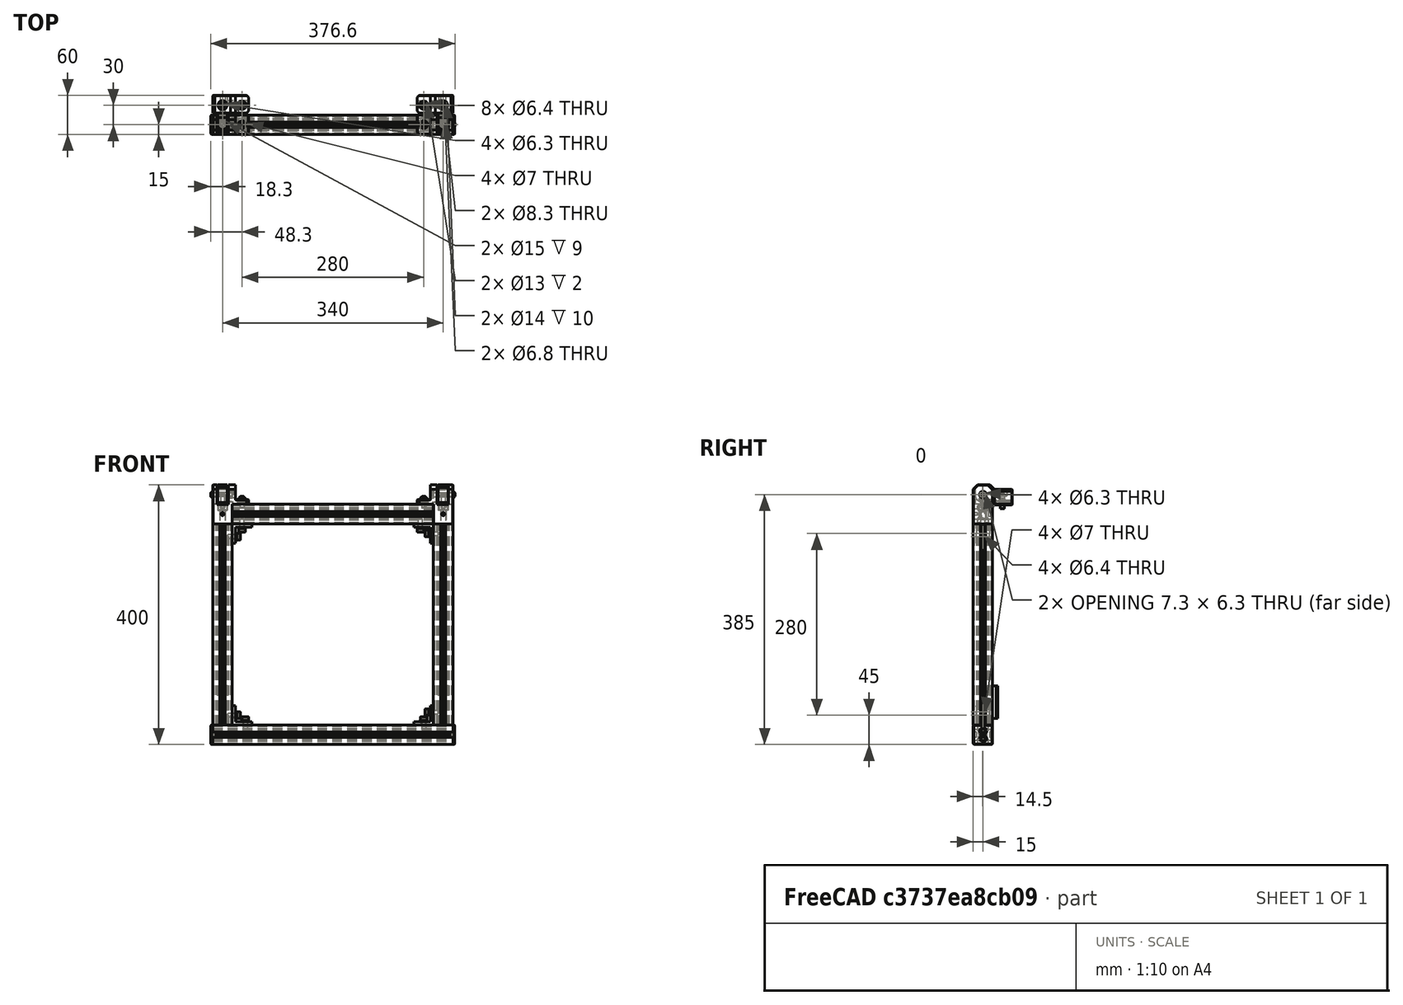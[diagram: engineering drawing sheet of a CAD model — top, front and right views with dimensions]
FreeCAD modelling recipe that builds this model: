
FCSTD DOCUMENT  (FreeCAD 0.19R24291 (Git))
Label: top-lid-assembly
License: Other
LicenseURL: GPL3
objects: Part::FeaturePython×32, Part::Feature×16, App::Part×1
note: 48 computed .brp shape members not serialized (recipe doc carries the construction recipe); baked Part::Feature solids carry a one-line shape summary decoded from their .brp

FEATURE [Part::Feature] Extrude002002003001  label="3030-370mm-top-lid-001"
  Placement = pos=(-3e-15,0,15) rot=(0,1,0;1.5708rad)
  shape: bbox 370 x 30 x 30 mm, 95 faces (baked)
FEATURE [Part::Feature] Extrude002002004001  label="3030-310mm-top-lid-001"
  Placement = pos=(15,0,30) rot=(0,0,1;0rad)
  shape: bbox 30 x 30 x 310 mm, 95 faces (baked)
FEATURE [Part::Feature] Extrude002002004002  label="3030-310mm-top-lid-002"
  Placement = pos=(355,0,30) rot=(0,0,1;0rad)
  shape: bbox 30 x 30 x 310 mm, 95 faces (baked)
FEATURE [Part::Feature] Extrude002002004003  label="3030-310mm-top-lid-003"
  Placement = pos=(340,0,355) rot=(0,-1,0;1.5708rad)
  shape: bbox 310 x 30 x 30 mm, 95 faces (baked)
FEATURE [Part::Feature] Chamfer002001010001
  Placement = pos=(30,45,385) rot=(0,0.707107,-0.707107;3.14159rad)
  shape: bbox 55 x 57 x 31 mm, 55 faces (baked)
FEATURE [Part::Feature] Chamfer002001012001
  Placement = pos=(30,15,370) rot=(0,0.707107,-0.707107;3.14159rad)
  shape: bbox 55 x 30 x 65 mm, 86 faces (baked)
FEATURE [Part::Feature] Part__Mirroring001001  label="Chamfer002001012001 (Mirror #2)001"
  Placement = pos=(340,15,370) rot=(0,0.707107,-0.707107;3.14159rad)
  shape: bbox 55 x 30 x 65 mm, 86 faces (baked)
FEATURE [Part::Feature] Part__Mirroring001002  label="Chamfer002001010001 (Mirror #1)001"
  Placement = pos=(340,45,385) rot=(0,0.707107,-0.707107;3.14159rad)
  shape: bbox 55 x 57 x 31 mm, 55 faces (baked)
FEATURE [Part::FeaturePython] Screw  label="M8x30-Screw"  # Fasteners workbench fastener (typed FeaturePython)
  Placement = pos=(355,1.23e-13,361) rot=(0,0,1;0rad)
  baseObject = -> Part__Mirroring001001 [Edge94]
  diameter = 8
  invert = false
  length = 6
  lengthCustom = 30
  matchOuter = true
  offset = 0
  thread = false
  type = 33
FEATURE [Part::FeaturePython] Screw001  label="M8x30-Screw001"  # Fasteners workbench fastener (typed FeaturePython)
  Placement = pos=(15,7.82e-14,361) rot=(0,0,1;0rad)
  baseObject = -> Chamfer002001012001 [Edge94]
  diameter = 8
  invert = true
  length = 6
  lengthCustom = 30
  matchOuter = true
  offset = 0
  thread = false
  type = 33
FEATURE [Part::FeaturePython] Washer  label="M6-Washer"  # Fasteners workbench fastener (typed FeaturePython)
  Placement = pos=(325,1.23e-13,377) rot=(0,0,1;0rad)
  baseObject = -> Part__Mirroring001001 [Edge130]
  diameter = 2
  invert = true
  matchOuter = true
  offset = 0
  type = 4
FEATURE [Part::FeaturePython] Washer001  label="M6-Washer001"  # Fasteners workbench fastener (typed FeaturePython)
  Placement = pos=(45,8.2e-14,377) rot=(0,0,1;0rad)
  baseObject = -> Chamfer002001012001 [Edge130]
  diameter = 2
  invert = false
  matchOuter = true
  offset = 0
  type = 4
FEATURE [Part::FeaturePython] Screw002  label="M6x14-Screw"  # Fasteners workbench fastener (typed FeaturePython)
  Placement = pos=(45,8.2e-14,378.8) rot=(0,0,1;0rad)
  baseObject = -> Washer001 [Edge1]
  diameter = 4
  invert = false
  length = 2
  lengthCustom = 14
  matchOuter = true
  offset = 0
  thread = false
  type = 39
FEATURE [Part::FeaturePython] Screw003  label="M6x14-Screw001"  # Fasteners workbench fastener (typed FeaturePython)
  Placement = pos=(325,1.23e-13,378.8) rot=(0,0,1;0rad)
  baseObject = -> Washer [Edge1]
  diameter = 4
  invert = false
  length = 2
  lengthCustom = 14
  matchOuter = true
  offset = 0
  thread = false
  type = 39
FEATURE [Part::FeaturePython] Nut  label="M6-Nut"  # Fasteners workbench fastener (typed FeaturePython)
  Placement = pos=(30,8.5e-14,385) rot=(0,-1,0;1.5708rad)
  baseObject = -> Chamfer002001012001 [Edge177]
  diameter = 8
  invert = false
  matchOuter = true
  offset = 0
  thread = false
  type = 7
FEATURE [Part::FeaturePython] Nut001  label="M6-Nut001"  # Fasteners workbench fastener (typed FeaturePython)
  Placement = pos=(340,1.28e-13,385) rot=(0,-1,0;1.5708rad)
  baseObject = -> Part__Mirroring001001 [Edge177]
  diameter = 8
  invert = false
  matchOuter = true
  offset = 0
  thread = false
  type = 7
FEATURE [Part::FeaturePython] Screw004  label="M6x10-Screw"  # Fasteners workbench fastener (typed FeaturePython)
  Placement = pos=(5e-14,8.5e-14,385) rot=(0,-1,0;1.5708rad)
  baseObject = -> Chamfer002001012001 [Edge70]
  diameter = 4
  invert = false
  length = 0
  lengthCustom = 10
  matchOuter = true
  offset = 0
  thread = false
  type = 39
FEATURE [Part::FeaturePython] Screw005  label="M6x10-Screw001"  # Fasteners workbench fastener (typed FeaturePython)
  Placement = pos=(370,1.32e-13,385) rot=(0,1,0;1.5708rad)
  baseObject = -> Part__Mirroring001001 [Edge70]
  diameter = 4
  invert = true
  length = 0
  lengthCustom = 10
  matchOuter = true
  offset = 0
  thread = false
  type = 39
FEATURE [Part::FeaturePython] Washer004  label="M6-Washer004"  # Fasteners workbench fastener (typed FeaturePython)
  Placement = pos=(325,30,374) rot=(0,0,1;0rad)
  baseObject = -> Part__Mirroring001002 [Edge130]
  diameter = 7
  invert = false
  matchOuter = true
  offset = 0
  type = 3
FEATURE [Part::FeaturePython] Washer005  label="M6-Washer005"  # Fasteners workbench fastener (typed FeaturePython)
  Placement = pos=(45,30,374) rot=(0,0,1;0rad)
  baseObject = -> Chamfer002001010001 [Edge130]
  diameter = 7
  invert = true
  matchOuter = true
  offset = 0
  type = 3
FEATURE [Part::FeaturePython] Screw008  label="M6x12-Screw"  # Fasteners workbench fastener (typed FeaturePython)
  Placement = pos=(325,30,375.8) rot=(0,0,1;0rad)
  baseObject = -> Washer004 [Edge1]
  diameter = 4
  invert = false
  length = 1
  lengthCustom = 12
  matchOuter = true
  offset = 0
  thread = false
  type = 39
FEATURE [Part::FeaturePython] Screw009  label="M6x12-Screw001"  # Fasteners workbench fastener (typed FeaturePython)
  Placement = pos=(45,30,375.8) rot=(0,0,1;0rad)
  baseObject = -> Washer005 [Edge1]
  diameter = 4
  invert = false
  length = 1
  lengthCustom = 12
  matchOuter = true
  offset = 0
  thread = false
  type = 39
FEATURE [Part::FeaturePython] Screw010  label="M6x20-Screw"  # Fasteners workbench fastener (typed FeaturePython)
  Placement = pos=(355,30,383) rot=(0,0,1;0rad)
  baseObject = -> Part__Mirroring001002 [Edge133]
  diameter = 4
  invert = false
  length = 4
  lengthCustom = 20
  matchOuter = true
  offset = 0
  thread = false
  type = 39
FEATURE [Part::FeaturePython] Screw011  label="M6x20-Screw001"  # Fasteners workbench fastener (typed FeaturePython)
  Placement = pos=(15,30,383) rot=(0,0,1;0rad)
  baseObject = -> Chamfer002001010001 [Edge133]
  diameter = 4
  invert = true
  length = 4
  lengthCustom = 20
  matchOuter = true
  offset = 0
  thread = false
  type = 39
FEATURE [Part::Feature] Part__Feature112001073  label="L-corner-bracket007"
  Placement = pos=(340,7.8e-14,340) rot=(0.57735,0.57735,-0.57735;4.18879rad)
  shape: bbox 30 x 20 x 30 mm, 10 faces (baked)
FEATURE [Part::Feature] Part__Feature112001074  label="L-corner-bracket008"
  Placement = pos=(30,7.8e-14,340) rot=(0.707107,0.707107,0;3.14159rad)
  shape: bbox 30 x 20 x 30 mm, 10 faces (baked)
FEATURE [Part::Feature] Part__Feature112001075  label="L-corner-bracket009"
  Placement = pos=(30,7.8e-14,30) rot=(0.57735,0.57735,0.57735;2.0944rad)
  shape: bbox 30 x 20 x 30 mm, 10 faces (baked)
FEATURE [Part::Feature] Part__Feature112001076  label="L-corner-bracket010"
  Placement = pos=(340,7.8e-14,30) rot=(0,0,1;1.5708rad)
  shape: bbox 30 x 20 x 30 mm, 10 faces (baked)
FEATURE [Part::FeaturePython] Washer006  label="M6-Washer006"  # Fasteners workbench fastener (typed FeaturePython)
  Placement = pos=(50,7.4e-14,35) rot=(0,0,1;0rad)
  baseObject = -> Part__Feature112001075 [Edge1]
  diameter = 2
  invert = true
  matchOuter = false
  offset = 0
  type = 4
FEATURE [Part::FeaturePython] Washer007  label="M6-Washer007"  # Fasteners workbench fastener (typed FeaturePython)
  Placement = pos=(35,7.7e-14,45) rot=(0,1,0;1.5708rad)
  baseObject = -> Part__Feature112001075 [Edge7]
  diameter = 2
  invert = true
  matchOuter = false
  offset = 0
  type = 4
FEATURE [Part::FeaturePython] Washer008  label="M6-Washer008"  # Fasteners workbench fastener (typed FeaturePython)
  Placement = pos=(325,7.5e-14,35) rot=(0,0,1;0rad)
  baseObject = -> Part__Feature112001076 [Edge7]
  diameter = 2
  invert = true
  matchOuter = false
  offset = 0
  type = 4
FEATURE [Part::FeaturePython] Washer009  label="M6-Washer009"  # Fasteners workbench fastener (typed FeaturePython)
  Placement = pos=(335,7.7e-14,50) rot=(0,-1,0;1.5708rad)
  baseObject = -> Part__Feature112001076 [Edge4]
  diameter = 2
  invert = true
  matchOuter = false
  offset = 0
  type = 4
FEATURE [Part::FeaturePython] Washer010  label="M6-Washer010"  # Fasteners workbench fastener (typed FeaturePython)
  Placement = pos=(320,7.9e-14,335) rot=(1,0,0;3.14159rad)
  baseObject = -> Part__Feature112001073 [Edge4]
  diameter = 2
  invert = true
  matchOuter = false
  offset = 0
  type = 4
FEATURE [Part::FeaturePython] Washer011  label="M6-Washer011"  # Fasteners workbench fastener (typed FeaturePython)
  Placement = pos=(335,8.1e-14,325) rot=(0,-1,0;1.5708rad)
  baseObject = -> Part__Feature112001073 [Edge7]
  diameter = 2
  invert = true
  matchOuter = false
  offset = 0
  type = 4
FEATURE [Part::FeaturePython] Washer012  label="M6-Washer012"  # Fasteners workbench fastener (typed FeaturePython)
  Placement = pos=(35,7.9e-14,320) rot=(0,1,0;1.5708rad)
  baseObject = -> Part__Feature112001074 [Edge1]
  diameter = 2
  invert = true
  matchOuter = false
  offset = 0
  type = 4
FEATURE [Part::FeaturePython] Washer013  label="M6-Washer013"  # Fasteners workbench fastener (typed FeaturePython)
  Placement = pos=(45,8.1e-14,335) rot=(1,0,0;3.14159rad)
  baseObject = -> Part__Feature112001074 [Edge7]
  diameter = 2
  invert = true
  matchOuter = false
  offset = 0
  type = 4
FEATURE [Part::FeaturePython] Screw012  label="M6x14-Screw015"  # Fasteners workbench fastener (typed FeaturePython)
  Placement = pos=(325,7.5e-14,36.8) rot=(0,0,1;0rad)
  baseObject = -> Washer008 [Edge1]
  diameter = 7
  invert = false
  length = 3
  lengthCustom = 14
  matchOuter = false
  offset = 0
  thread = false
  type = 33
FEATURE [Part::FeaturePython] Screw013  label="M6x14-Screw016"  # Fasteners workbench fastener (typed FeaturePython)
  Placement = pos=(333.2,7.7e-14,50) rot=(0,-1,0;1.5708rad)
  baseObject = -> Washer009 [Edge1]
  diameter = 7
  invert = false
  length = 3
  lengthCustom = 14
  matchOuter = false
  offset = 0
  thread = false
  type = 33
FEATURE [Part::FeaturePython] Screw014  label="M6x14-Screw013"  # Fasteners workbench fastener (typed FeaturePython)
  Placement = pos=(36.8,7.7e-14,45) rot=(0,1,0;1.5708rad)
  baseObject = -> Washer007 [Edge1]
  diameter = 7
  invert = false
  length = 3
  lengthCustom = 14
  matchOuter = false
  offset = 0
  thread = false
  type = 33
FEATURE [Part::FeaturePython] Screw015  label="M6x14-Screw014"  # Fasteners workbench fastener (typed FeaturePython)
  Placement = pos=(50,7.4e-14,36.8) rot=(0,0,1;0rad)
  baseObject = -> Washer006 [Edge1]
  diameter = 7
  invert = false
  length = 3
  lengthCustom = 14
  matchOuter = false
  offset = 0
  thread = false
  type = 33
FEATURE [Part::FeaturePython] Screw016  label="M6x14-Screw011"  # Fasteners workbench fastener (typed FeaturePython)
  Placement = pos=(36.8,7.9e-14,320) rot=(0,1,0;1.5708rad)
  baseObject = -> Washer012 [Edge1]
  diameter = 7
  invert = false
  length = 3
  lengthCustom = 14
  matchOuter = false
  offset = 0
  thread = false
  type = 33
FEATURE [Part::FeaturePython] Screw017  label="M6x14-Screw012"  # Fasteners workbench fastener (typed FeaturePython)
  Placement = pos=(45,8.1e-14,333.2) rot=(1,0,0;3.14159rad)
  baseObject = -> Washer013 [Edge1]
  diameter = 7
  invert = false
  length = 3
  lengthCustom = 14
  matchOuter = false
  offset = 0
  thread = false
  type = 33
FEATURE [Part::FeaturePython] Screw018  label="M6x14-Screw010"  # Fasteners workbench fastener (typed FeaturePython)
  Placement = pos=(320,7.9e-14,333.2) rot=(1,0,0;3.14159rad)
  baseObject = -> Washer010 [Edge1]
  diameter = 7
  invert = false
  length = 3
  lengthCustom = 14
  matchOuter = false
  offset = 0
  thread = false
  type = 33
FEATURE [Part::FeaturePython] Screw019  label="M6x14-Screw009"  # Fasteners workbench fastener (typed FeaturePython)
  Placement = pos=(333.2,8.1e-14,325) rot=(0,-1,0;1.5708rad)
  baseObject = -> Washer011 [Edge1]
  diameter = 7
  invert = false
  length = 3
  lengthCustom = 14
  matchOuter = false
  offset = 0
  thread = false
  type = 33
FEATURE [Part::Feature] Chamfer002001018001001001
  Placement = pos=(15,15,90) rot=(1,0,0;3.14159rad)
  shape: bbox 16 x 16 x 60 mm, 19 faces (baked)
FEATURE [Part::Feature] Chamfer002001018001001002
  Placement = pos=(355,15,90) rot=(1,0,0;3.14159rad)
  shape: bbox 16 x 16 x 60 mm, 19 faces (baked)
FEATURE [Part::Feature] Fusion003012003006001
  Placement = pos=(-3.3e-15,0,15) rot=(0.707107,0,0.707107;3.14159rad)
  shape: bbox 10 x 30 x 30 mm, 385 faces (baked)
FEATURE [Part::Feature] Fusion003012003006002
  Placement = pos=(370,0,15) rot=(-0.707107,0,0.707107;3.14159rad)
  shape: bbox 10 x 30 x 30 mm, 385 faces (baked)
FEATURE [App::Part] Part  label="top-lod"
  Group = -> [Extrude002002003001,Extrude002002004001,Extrude002002004002,Extrude002002004003,Washer005,Screw009,Screw011,Chamfer002001010001,Screw001,Washer001,Screw002,Nut,Screw004,Chamfer002001012001,Screw,Washer,Screw003,Nut001,Screw005,Part__Mirroring001001,Washer004,Screw008,Screw010,Part__Mirroring001002,Washer011,Washer010,Screw019,Screw018,Part__Feature112001073,Screw016,Washer012,Washer013,Screw017,+15 more]
  Origin = -> Origin
